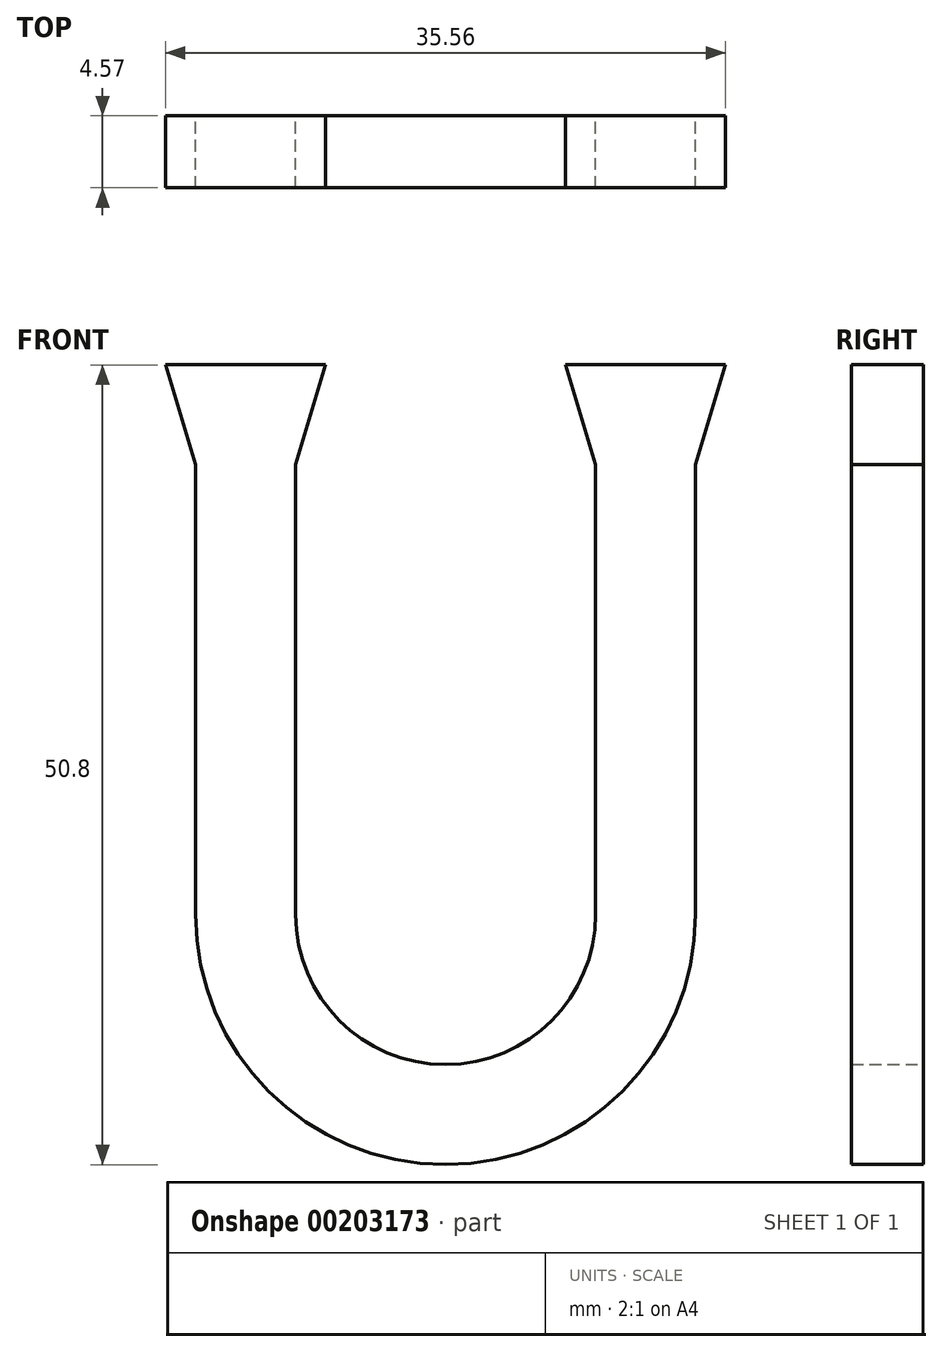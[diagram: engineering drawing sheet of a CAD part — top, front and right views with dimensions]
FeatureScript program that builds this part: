
annotation { "Feature Type Name" : "Feature", "Feature Type Description" : "" }
export const myFeature = defineFeature(function(context is Context, id is Id, definition is map)
    precondition{}
    {
        {
            var Q0;
            Q0=qCreatedBy(makeId("Front.planeOp"),FACE);
            var sketch = newSketch(context, id + "F0", { "sketchPlane" : qUnion([Q0])});
            skArc(sketch, "E0", {"start": v(-15.88, 0) * mm, "mid": v(0, -15.88) * mm, "end": v(15.88, 0) * mm});
            skLineSegment(sketch, "E1.top", {"start": v(-15.88, 34.92) * mm, "end": v(-9.52, 34.92) * mm});
            skLineSegment(sketch, "E1.left", {"start": v(-15.88, 0) * mm, "end": v(-15.88, 28.58) * mm});
            skLineSegment(sketch, "E1.right", {"start": v(-9.53, 0) * mm, "end": v(-9.52, 28.58) * mm});
            skLineSegment(sketch, "E2.top", {"start": v(15.87, 34.92) * mm, "end": v(9.52, 34.92) * mm});
            skLineSegment(sketch, "E2.left", {"start": v(15.88, 0) * mm, "end": v(15.87, 28.57) * mm});
            skLineSegment(sketch, "E2.right", {"start": v(9.52, 0) * mm, "end": v(9.52, 28.58) * mm});
            skArc(sketch, "E3", {"start": v(-9.53, 0) * mm, "mid": v(0, -9.53) * mm, "end": v(9.53, 0) * mm});
            skLineSegment(sketch, "E4", {"start": v(-15.87, 28.58) * mm, "end": v(-17.78, 34.93) * mm});
            skLineSegment(sketch, "E5", {"start": v(-17.78, 34.92) * mm, "end": v(-15.88, 34.92) * mm});
            skLineSegment(sketch, "E6", {"start": v(-9.52, 34.92) * mm, "end": v(-7.62, 34.92) * mm});
            skLineSegment(sketch, "E7", {"start": v(-7.62, 34.93) * mm, "end": v(-9.53, 28.58) * mm});
            skLineSegment(sketch, "E8", {"start": v(9.52, 34.92) * mm, "end": v(7.62, 34.92) * mm});
            skLineSegment(sketch, "E9", {"start": v(7.62, 34.92) * mm, "end": v(9.52, 28.58) * mm});
            skLineSegment(sketch, "E10", {"start": v(15.87, 34.92) * mm, "end": v(17.78, 34.92) * mm});
            skLineSegment(sketch, "E11", {"start": v(17.78, 34.92) * mm, "end": v(15.88, 28.57) * mm});
            skSolve(sketch);
        }
        {
            var Q0;
            Q0 = qSketchRegion(id + "F0", true);
            extrude(context, id + "F1", {"entities" : qUnion([Q0]), "depth" : 4.57 * mm});
        }
    });
